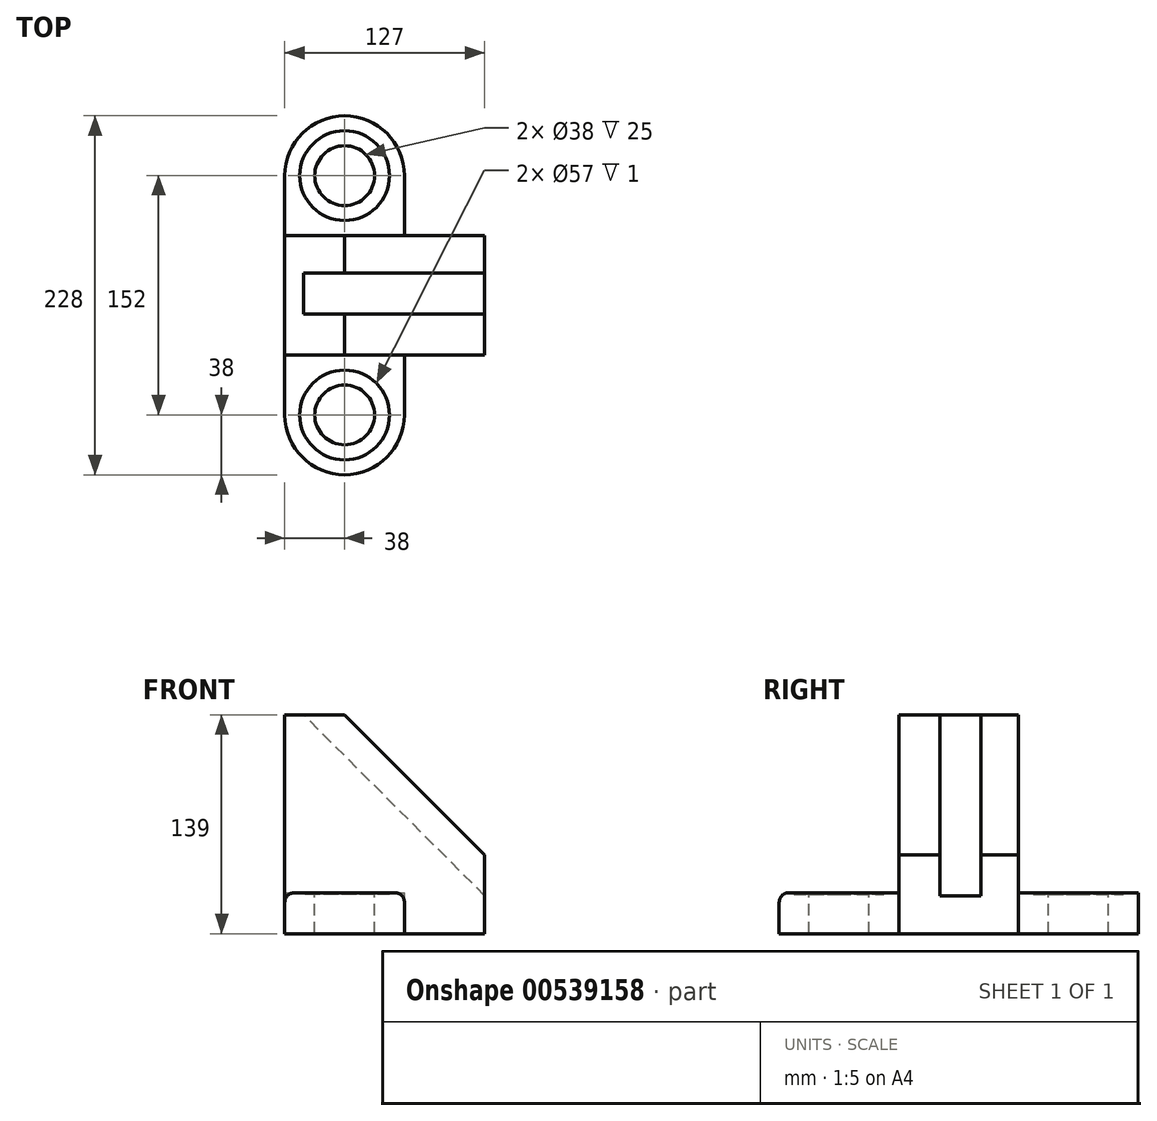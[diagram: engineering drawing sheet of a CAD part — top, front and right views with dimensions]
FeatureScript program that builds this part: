
annotation { "Feature Type Name" : "Feature", "Feature Type Description" : "" }
export const myFeature = defineFeature(function(context is Context, id is Id, definition is map)
    precondition{}
    {
        {
            var Q0;
            Q0=qCreatedBy(makeId("Top.planeOp"),FACE);
            var sketch = newSketch(context, id + "F0", { "sketchPlane" : qUnion([Q0])});
            skLineSegment(sketch, "E0.bottom", {"start": v(0, 0) * mm, "end": v(127, 0) * mm});
            skLineSegment(sketch, "E0.top", {"start": v(0, 76) * mm, "end": v(127, 76) * mm});
            skLineSegment(sketch, "E0.left", {"start": v(0, 0) * mm, "end": v(0, 76) * mm});
            skLineSegment(sketch, "E0.right", {"start": v(127, 0) * mm, "end": v(127, 76) * mm});
            skPoint(sketch, "E1.endSnap0", {"position": v(0, 38) * mm});
            skSolve(sketch);
        }
        {
            var Q0;
            Q0 = qSketchRegion(id + "F0", true);
            extrude(context, id + "F1", {"entities" : qUnion([Q0]), "depth" : 200 * mm, "offsetDistance" : 25 * mm});
        }
        {
            var Q0;
            Q0=makeQuery(id+"F1.opExtrude","SWEPT_FACE",FACE,{"disambiguationData":[OSD([sQuery(id+"F0.wireOp",EDGE,"E0.bottom")])]});
            var sketch = newSketch(context, id + "F2", { "sketchPlane" : qUnion([Q0])});
            skLineSegment(sketch, "E2", {"start": v(127, 50) * mm, "end": v(0, 177) * mm});
            skLineSegment(sketch, "E3", {"start": v(0, 139) * mm, "end": v(38, 139) * mm});
            skLineSegment(sketch, "E4", {"start": v(0, 177) * mm, "end": v(191.21, -14.21) * mm});
            skSolve(sketch);
        }
        {
            var Q0;
            {var subQ0=sQuery(id+"F0.wireOp",EDGE,"E0.bottom");var subQ1=makeQuery(id+"F1.opExtrude","CAP_EDGE",EDGE,{"disambiguationData":[OSD([subQ0])],"isStart":false});Q0=makeQuery(id+"F2.imprint","IMPRINT",FACE,{"disambiguationData":[TD([[makeQuery(id+"F2.imprint","IMPRINT",EDGE,{"derivedFrom":subQ1}),-1.0]])]});}
            var Q1;
            {var subQ3=sQuery(id+"F2.wireOp",EDGE,"E3");Q1=makeQuery(id+"F2.imprint","IMPRINT",FACE,{"disambiguationData":[TD([[makeQuery(id+"F2.imprint","IMPRINT",EDGE,{"derivedFrom":subQ3}),1.0]])]});}
            extrude(context, id + "F3", {"entities" : qUnion([Q0, Q1]), "operationType" : NewBodyOperationType.REMOVE, "endBound" : BoundingType.THROUGH_ALL, "oppositeDirection" : true, "depth" : 25 * mm, "offsetDistance" : 25 * mm});
        }
        {
            var Q0;
            Q0=makeQuery(id+"F3.boolean.opBoolean","COPY",FACE,{"derivedFrom":makeQuery(id+"F3.opExtrude","SWEPT_FACE",FACE,{"disambiguationData":[OSD([sQuery(id+"F2.wireOp",EDGE,"E3")])]})});
            var sketch = newSketch(context, id + "F4", { "sketchPlane" : qUnion([Q0])});
            skLineSegment(sketch, "E5.bottom", {"start": v(38, 26) * mm, "end": v(12, 26) * mm});
            skLineSegment(sketch, "E5.top", {"start": v(38, 52) * mm, "end": v(12, 52) * mm});
            skLineSegment(sketch, "E5.left", {"start": v(38, 26) * mm, "end": v(38, 52) * mm});
            skLineSegment(sketch, "E5.right", {"start": v(12, 26) * mm, "end": v(12, 52) * mm});
            skSolve(sketch);
        }
        {
            var Q0;
            Q0=makeQuery(id+"F4.imprint","IMPRINT",FACE,{"disambiguationData":[TD([[makeQuery(id+"F4.imprint","IMPRINT",EDGE,{"derivedFrom":sQuery(id+"F4.wireOp",EDGE,"E5.bottom")}),-1.0]])]});
            var Q1;
            Q1=sQuery(id+"F2.wireOp",EDGE,"E4");
            sweep(context, id + "F5", {"operationType" : NewBodyOperationType.REMOVE, "profiles" : qUnion([Q0]), "path" : qUnion([Q1])});
        }
        {
            var Q0;
            Q0=makeQuery(id+"F1.opExtrude","SWEPT_FACE",FACE,{"disambiguationData":[OSD([sQuery(id+"F0.wireOp",EDGE,"E0.bottom")])]});
            var sketch = newSketch(context, id + "F6", { "sketchPlane" : qUnion([Q0])});
            skLineSegment(sketch, "E6.bottom", {"start": v(0, 0) * mm, "end": v(76, 0) * mm});
            skLineSegment(sketch, "E6.top", {"start": v(0, 26) * mm, "end": v(76, 26) * mm});
            skLineSegment(sketch, "E6.left", {"start": v(0, 0) * mm, "end": v(0, 26) * mm});
            skLineSegment(sketch, "E6.right", {"start": v(76, 0) * mm, "end": v(76, 26) * mm});
            skSolve(sketch);
        }
        {
            var Q0;
            Q0 = qSketchRegion(id + "F6", true);
            extrude(context, id + "F7", {"entities" : qUnion([Q0]), "operationType" : NewBodyOperationType.ADD, "depth" : 76 * mm, "offsetDistance" : 25 * mm});
        }
        {
            var Q0;
            Q0=makeQuery(id+"F7.opExtrude","CAP_EDGE",EDGE,{"disambiguationData":[OSD([sQuery(id+"F6.wireOp",EDGE,"E6.right")])],"isStart":false});
            var Q1;
            Q1=makeQuery(id+"F7.opExtrude","CAP_EDGE",EDGE,{"disambiguationData":[OSD([sQuery(id+"F6.wireOp",EDGE,"E6.left")])],"isStart":false});
            fillet(context, id + "F8", {"entities" : qUnion([Q0, Q1]), "radius" : 38 * mm, "tangentPropagation" : true, "allowEdgeOverflow" : false});
        }
        {
            var Q0;
            Q0=makeQuery(id+"F1.opExtrude","SWEPT_FACE",FACE,{"disambiguationData":[OSD([sQuery(id+"F0.wireOp",EDGE,"E0.top")])]});
            var sketch = newSketch(context, id + "F9", { "sketchPlane" : qUnion([Q0])});
            skLineSegment(sketch, "E7.bottom", {"start": v(0, 0) * mm, "end": v(-76, 0) * mm});
            skLineSegment(sketch, "E7.top", {"start": v(0, 26) * mm, "end": v(-76, 26) * mm});
            skLineSegment(sketch, "E7.left", {"start": v(0, 0) * mm, "end": v(0, 26) * mm});
            skLineSegment(sketch, "E7.right", {"start": v(-76, 0) * mm, "end": v(-76, 26) * mm});
            skSolve(sketch);
        }
        {
            var Q0;
            Q0 = qSketchRegion(id + "F9", true);
            extrude(context, id + "F10", {"entities" : qUnion([Q0]), "operationType" : NewBodyOperationType.ADD, "depth" : 76 * mm, "offsetDistance" : 25 * mm});
        }
        {
            var Q0;
            Q0=makeQuery(id+"F10.opExtrude","CAP_EDGE",EDGE,{"disambiguationData":[OSD([sQuery(id+"F9.wireOp",EDGE,"E7.left")])],"isStart":false});
            var Q1;
            Q1=makeQuery(id+"F10.opExtrude","CAP_EDGE",EDGE,{"disambiguationData":[OSD([sQuery(id+"F9.wireOp",EDGE,"E7.right")])],"isStart":false});
            fillet(context, id + "F11", {"entities" : qUnion([Q0, Q1]), "radius" : 38 * mm, "tangentPropagation" : true, "allowEdgeOverflow" : false});
        }
        {
            var Q0;
            Q0=makeQuery(id+"F10.opExtrude","SWEPT_FACE",FACE,{"disambiguationData":[OSD([sQuery(id+"F9.wireOp",EDGE,"E7.top")])]});
            var sketch = newSketch(context, id + "F12", { "sketchPlane" : qUnion([Q0])});
            skCircle(sketch, "E8", {"center": v(38, 114) * mm, "radius": 28.5 * mm});
            skCircle(sketch, "E9", {"center": v(38, 114) * mm, "radius": 19 * mm});
            skSolve(sketch);
        }
        {
            var Q0;
            Q0=makeQuery(id+"F12.imprint","IMPRINT",FACE,{"disambiguationData":[TD([[makeQuery(id+"F12.imprint","IMPRINT",EDGE,{"derivedFrom":sQuery(id+"F12.wireOp",EDGE,"E9")}),1.0]])]});
            var Q1;
            Q1=makeQuery(id+"FI64LyHn0jINCfR_1.imprint","IMPRINT",FACE,{"disambiguationData":[TD([[makeQuery(id+"FI64LyHn0jINCfR_1.imprint","IMPRINT",EDGE,{"derivedFrom":sQuery(id+"FI64LyHn0jINCfR_1.wireOp",EDGE,"N4nHZHMn-ALKG-3PrP-qjwV-SayOugzacz2c")}),1.0]])]});
            extrude(context, id + "F13", {"entities" : qUnion([Q0, Q1]), "operationType" : NewBodyOperationType.REMOVE, "endBound" : BoundingType.THROUGH_ALL, "oppositeDirection" : true, "depth" : 25 * mm, "offsetDistance" : 25 * mm});
        }
        {
            var Q0;
            Q0=makeQuery(id+"FI64LyHn0jINCfR_1.imprint","IMPRINT",FACE,{"disambiguationData":[TD([[makeQuery(id+"FI64LyHn0jINCfR_1.imprint","IMPRINT",EDGE,{"derivedFrom":sQuery(id+"FI64LyHn0jINCfR_1.wireOp",EDGE,"WaURGeut-Rq7U-BFaY-Efcy-NrdPBiTNY8bW")}),1.0]])]});
            var Q1;
            Q1=makeQuery(id+"F12.imprint","IMPRINT",FACE,{"disambiguationData":[TD([[makeQuery(id+"F12.imprint","IMPRINT",EDGE,{"derivedFrom":sQuery(id+"F12.wireOp",EDGE,"E8")}),1.0]])]});
            extrude(context, id + "F14", {"entities" : qUnion([Q0, Q1]), "operationType" : NewBodyOperationType.REMOVE, "oppositeDirection" : true, "depth" : 1 * mm, "offsetDistance" : 25 * mm});
        }
        {
            var Q0;
            Q0=makeQuery(id+"F11.opFillet","BLEND_EDGE",EDGE,{"blendedFrom":[makeQuery(id+"F10.opExtrude","CAP_EDGE",EDGE,{"disambiguationData":[OSD([sQuery(id+"F9.wireOp",EDGE,"E7.right")])],"isStart":false}),makeQuery(id+"F10.opExtrude","SWEPT_FACE",FACE,{"disambiguationData":[OSD([sQuery(id+"F9.wireOp",EDGE,"E7.top")])]})],"blendedInto":[makeQuery(id+"F10.opExtrude","SWEPT_FACE",FACE,{"disambiguationData":[OSD([sQuery(id+"F9.wireOp",EDGE,"E7.top")])]})]});
            var Q1;
            Q1=makeQuery(id+"F8.opFillet","BLEND_EDGE",EDGE,{"blendedFrom":[makeQuery(id+"F7.opExtrude","CAP_EDGE",EDGE,{"disambiguationData":[OSD([sQuery(id+"F6.wireOp",EDGE,"E6.left")])],"isStart":false}),makeQuery(id+"F7.opExtrude","SWEPT_FACE",FACE,{"disambiguationData":[OSD([sQuery(id+"F6.wireOp",EDGE,"E6.top")])]})],"blendedInto":[makeQuery(id+"F7.opExtrude","SWEPT_FACE",FACE,{"disambiguationData":[OSD([sQuery(id+"F6.wireOp",EDGE,"E6.top")])]})]});
            fillet(context, id + "F15", {"entities" : qUnion([Q0, Q1]), "radius" : 6 * mm, "tangentPropagation" : true, "allowEdgeOverflow" : false});
        }
        {
            var Q0;
            Q0=makeQuery(id+"F7.opExtrude","SWEPT_FACE",FACE,{"disambiguationData":[OSD([sQuery(id+"F6.wireOp",EDGE,"E6.top")])]});
            var sketch = newSketch(context, id + "F16", { "sketchPlane" : qUnion([Q0])});
            skCircle(sketch, "E10", {"center": v(38, -38) * mm, "radius": 28.5 * mm});
            skCircle(sketch, "E11", {"center": v(38, -38) * mm, "radius": 19 * mm});
            skSolve(sketch);
        }
        {
            var Q0;
            Q0 = qSketchRegion(id + "F16", true);
            extrude(context, id + "F17", {"entities" : qUnion([Q0]), "operationType" : NewBodyOperationType.REMOVE, "oppositeDirection" : true, "depth" : 1 * mm, "offsetDistance" : 25 * mm});
        }
        {
            var Q0;
            Q0=makeQuery(id+"F17.boolean.opBoolean","SPLIT",FACE,{"disambiguationData":[TD([makeQuery(id+"F17.opExtrude","SWEPT_FACE",FACE,{"disambiguationData":[OSD([sQuery(id+"F16.wireOp",EDGE,"E11")])]})])],"derivedFrom":makeQuery(id+"F7.opExtrude","SWEPT_FACE",FACE,{"disambiguationData":[OSD([sQuery(id+"F6.wireOp",EDGE,"E6.top")])]})});
            extrude(context, id + "F18", {"entities" : qUnion([Q0]), "operationType" : NewBodyOperationType.REMOVE, "endBound" : BoundingType.UP_TO_NEXT, "oppositeDirection" : true, "depth" : 25 * mm, "offsetDistance" : 25 * mm});
        }
    });
